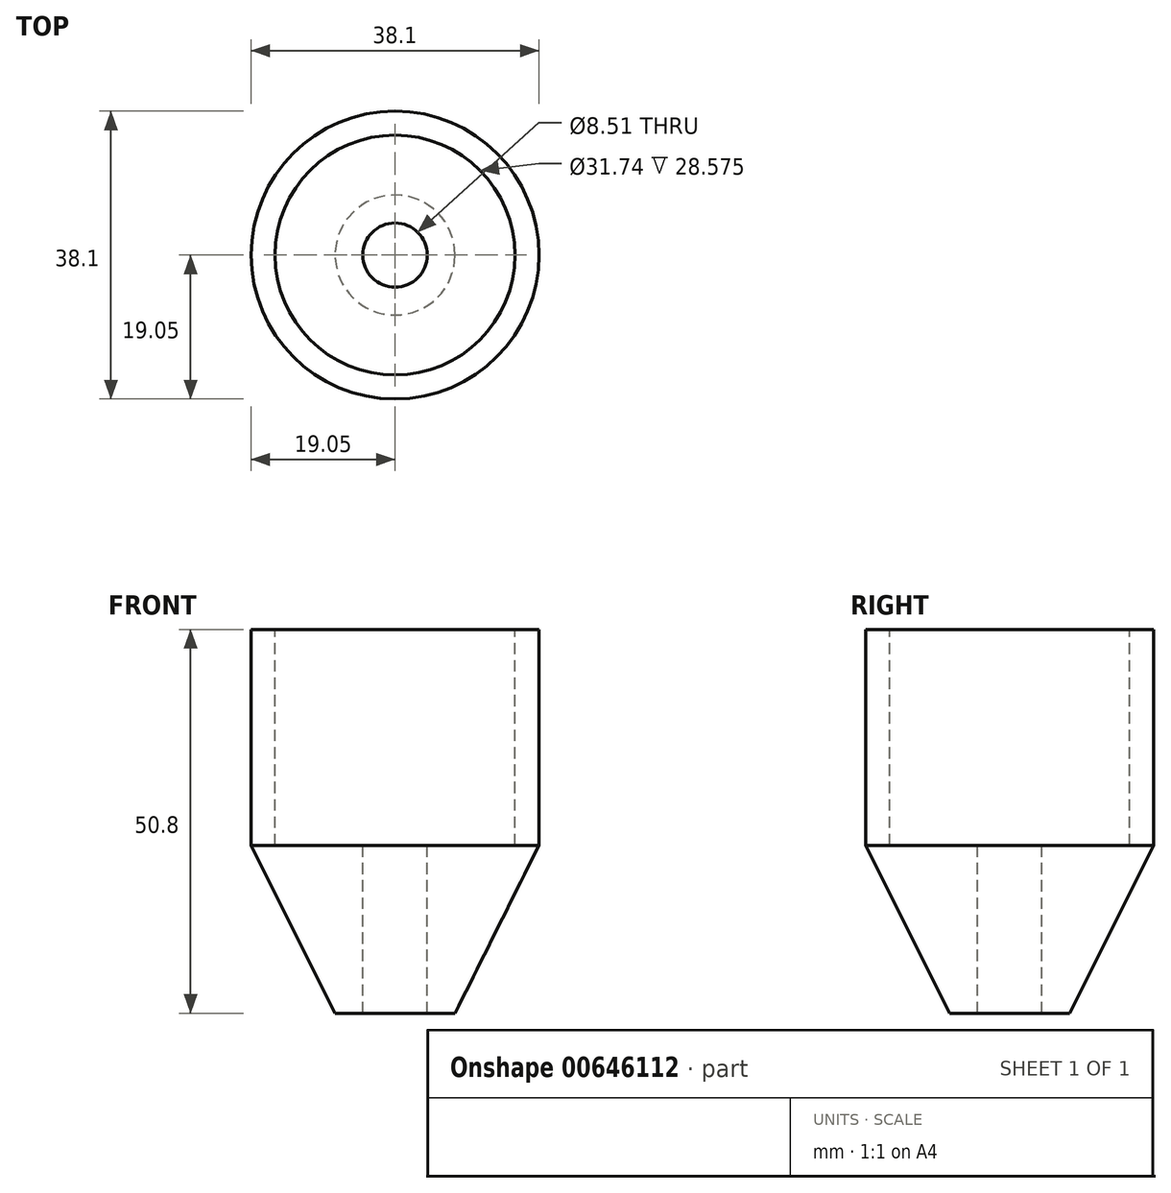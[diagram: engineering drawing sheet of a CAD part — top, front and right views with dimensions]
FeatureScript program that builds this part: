
annotation { "Feature Type Name" : "Feature", "Feature Type Description" : "" }
export const myFeature = defineFeature(function(context is Context, id is Id, definition is map)
    precondition{}
    {
        {
            var Q0;
            Q0=qCreatedBy(makeId("Top.planeOp"),FACE);
            cPlane(context, id + "F0", {"entities" : qUnion([Q0]), "cplaneType" : CPlaneType.OFFSET, "offset" : 22.22 * mm, "width" : 152.4 * mm, "height" : 152.4 * mm});
        }
        {
            var Q0;
            Q0=qCreatedBy(id+"F0.planeOp",FACE);
            var sketch = newSketch(context, id + "F1", { "sketchPlane" : qUnion([Q0])});
            skCircle(sketch, "E0", {"center": v(0, 0) * mm, "radius": 19.05 * mm});
            skSolve(sketch);
        }
        {
            var Q0;
            Q0=qCreatedBy(makeId("Top.planeOp"),FACE);
            var sketch = newSketch(context, id + "F2", { "sketchPlane" : qUnion([Q0])});
            skCircle(sketch, "E1", {"center": v(0, 0) * mm, "radius": 7.94 * mm});
            skSolve(sketch);
        }
        {
            var Q0;
            Q0=makeQuery(id+"F2.imprint","IMPRINT",FACE,{"disambiguationData":[TD([[makeQuery(id+"F2.imprint","IMPRINT",EDGE,{"derivedFrom":sQuery(id+"F2.wireOp",EDGE,"E1")}),1.0]])]});
            var Q1;
            Q1=makeQuery(id+"F1.imprint","IMPRINT",FACE,{"disambiguationData":[TD([[makeQuery(id+"F1.imprint","IMPRINT",EDGE,{"derivedFrom":sQuery(id+"F1.wireOp",EDGE,"E0")}),1.0]])]});
            loft(context, id + "F3", {"sheetProfilesArray" : [{ "sheetProfileEntities" : qUnion([Q0]) }, { "sheetProfileEntities" : qUnion([Q1]) }]});
        }
        {
            var Q0;
            Q0=qCreatedBy(id+"F0.planeOp",FACE);
            var sketch = newSketch(context, id + "F4", { "sketchPlane" : qUnion([Q0])});
            skCircle(sketch, "E2", {"center": v(0, 0) * mm, "radius": 4.25 * mm});
            skSolve(sketch);
        }
        {
            var Q0;
            Q0 = qSketchRegion(id + "F4", true);
            extrude(context, id + "F5", {"entities" : qUnion([Q0]), "operationType" : NewBodyOperationType.REMOVE, "oppositeDirection" : true, "depth" : 22.22 * mm, "offsetDistance" : 25.4 * mm});
        }
        {
            var Q0;
            Q0 = qSketchRegion(id + "F1", true);
            extrude(context, id + "F6", {"entities" : qUnion([Q0]), "operationType" : NewBodyOperationType.ADD, "depth" : 28.57 * mm, "offsetDistance" : 25.4 * mm});
        }
        {
            var Q0;
            Q0=makeQuery(id+"F6.opExtrude","CAP_FACE",FACE,{"disambiguationData":[OSD([sQuery(id+"F1.wireOp",EDGE,"E0")])],"isStart":false});
            var sketch = newSketch(context, id + "F7", { "sketchPlane" : qUnion([Q0])});
            skCircle(sketch, "E3", {"center": v(0, 0) * mm, "radius": 15.87 * mm});
            skSolve(sketch);
        }
        {
            var Q0;
            Q0=makeQuery(id+"F7.imprint","IMPRINT",FACE,{"disambiguationData":[TD([[makeQuery(id+"F7.imprint","IMPRINT",EDGE,{"derivedFrom":sQuery(id+"F7.wireOp",EDGE,"E3")}),1.0]])]});
            var Q1;
            Q1=sQuery(id+"F7.wireOp",EDGE,"E3");
            extrude(context, id + "F8", {"entities" : qUnion([Q0]), "operationType" : NewBodyOperationType.REMOVE, "surfaceEntities" : qUnion([Q1]), "oppositeDirection" : true, "depth" : 28.57 * mm, "offsetDistance" : 25.4 * mm});
        }
    });
